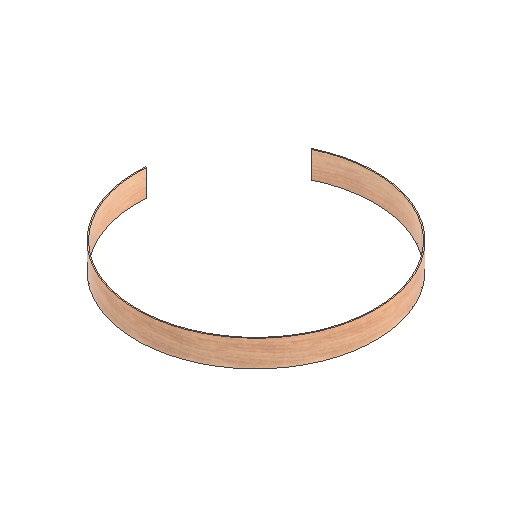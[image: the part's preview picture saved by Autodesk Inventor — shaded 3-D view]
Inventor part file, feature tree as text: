
AUTODESK INVENTOR PART (.ipt)
format: ipt  version: 2021 (Build 250183000, 183)  size: 137,216 bytes
history: native  units: mm
features: other x4, extrude x2, sketch x2, reference x2
ambient origin geometry x8: Origin, YZ Plane, XZ Plane, XY Plane, X Axis, Y Axis, Z Axis, Center Point
bodies: Solid1 (feature_tree)
feature tree (10):
  extrude  "Extrusion1"  Depth=892.0mm
  extrude  "Extrusion2"  Depth=100.0mm TaperAngle=0.0deg
  sketch  "Sketch1"  dims[d0=900.0mm d1=892.0mm]
  sketch  "Sketch2"  dims[d2=100.0mm d3=0.0mm d4=100.0mm d5=0.0mm]
  reference  "Reference1"
  reference  "Reference2"
  other  "Full Scale Assembly.iam"
  other  "Disc B Assembly:1"
  other  "Platform B1:1"
  other  "Platform B4:1"
